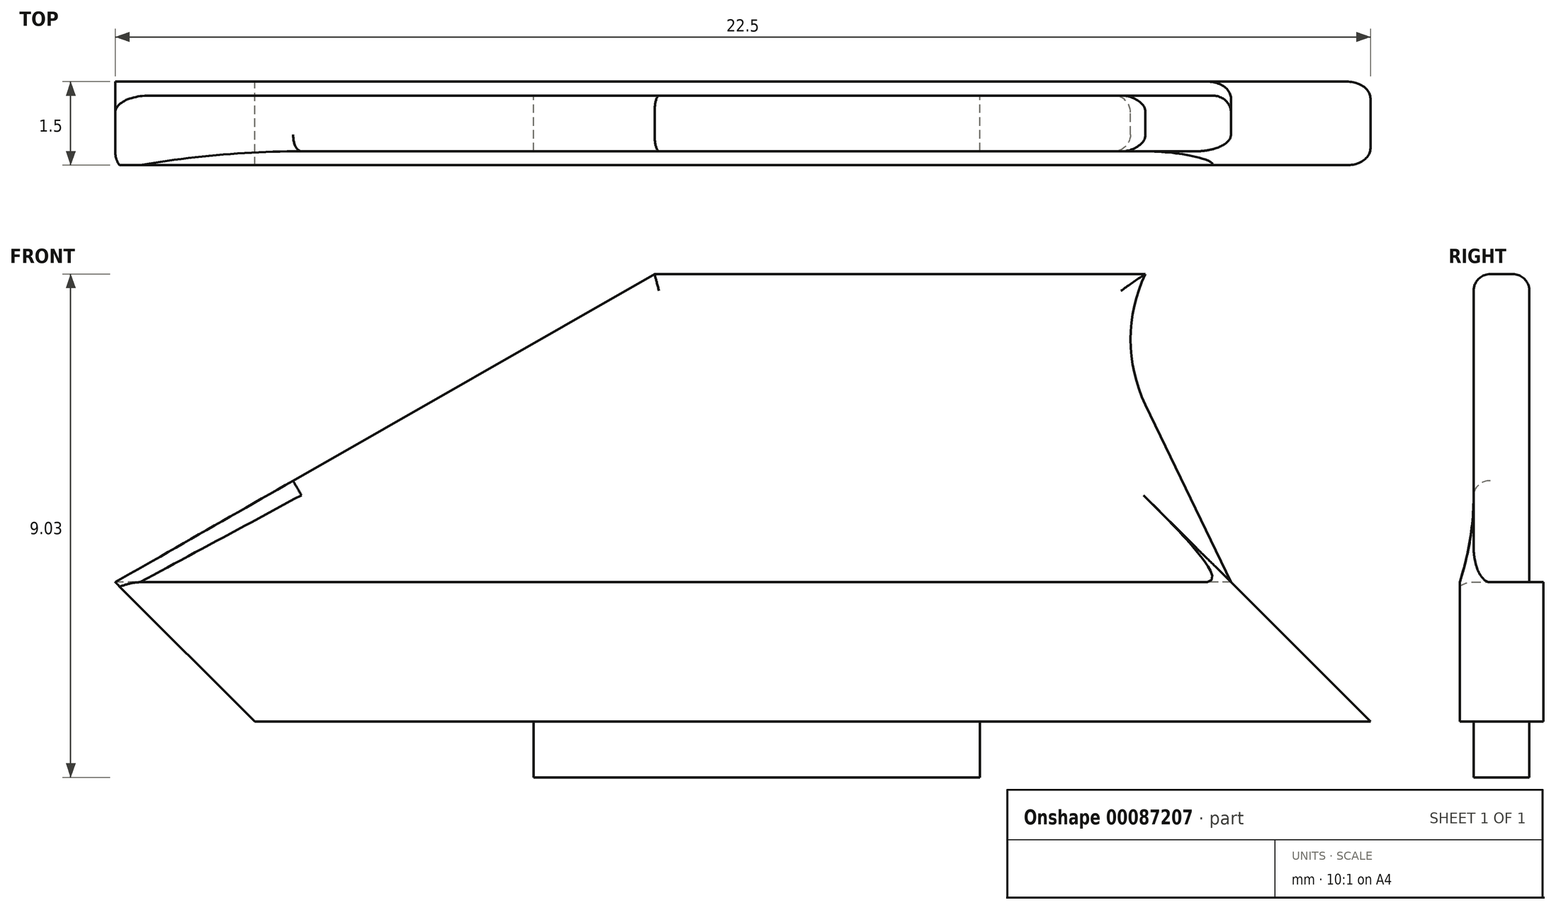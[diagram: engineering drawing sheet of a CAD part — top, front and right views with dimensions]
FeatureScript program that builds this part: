
annotation { "Feature Type Name" : "Feature", "Feature Type Description" : "" }
export const myFeature = defineFeature(function(context is Context, id is Id, definition is map)
    precondition{}
    {
        {
            var Q0;
            Q0=qCreatedBy(makeId("Front.planeOp"),FACE);
            var sketch = newSketch(context, id + "F0", { "sketchPlane" : qUnion([Q0])});
            skLineSegment(sketch, "E0", {"start": v(0, 0) * mm, "end": v(-20, 0) * mm});
            skLineSegment(sketch, "E1", {"start": v(-22.5, 2.5) * mm, "end": v(-20, 0) * mm});
            skLineSegment(sketch, "E2", {"start": v(-22.5, 2.5) * mm, "end": v(-2.5, 2.5) * mm});
            skLineSegment(sketch, "E3", {"start": v(-2.5, 2.5) * mm, "end": v(0, 0) * mm});
            skSolve(sketch);
        }
        {
            var Q0;
            Q0 = qSketchRegion(id + "F0", true);
            extrude(context, id + "F1", {"entities" : qUnion([Q0]), "endBound" : BoundingType.SYMMETRIC, "depth" : 1.5 * mm});
        }
        {
            var Q0;
            Q0=makeQuery(id+"F1.opExtrude","CAP_EDGE",EDGE,{"disambiguationData":[OSD([sQuery(id+"F0.wireOp",EDGE,"E3")])],"isStart":true});
            var Q1;
            Q1=makeQuery(id+"F1.opExtrude","CAP_EDGE",EDGE,{"disambiguationData":[OSD([sQuery(id+"F0.wireOp",EDGE,"E3")])],"isStart":false});
            fillet(context, id + "F2", {"entities" : qUnion([Q0, Q1]), "radius" : .3 * mm, "tangentPropagation" : true, "allowEdgeOverflow" : false});
        }
        {
            var Q0;
            Q0=qCreatedBy(makeId("Front.planeOp"),FACE);
            var sketch = newSketch(context, id + "F3", { "sketchPlane" : qUnion([Q0])});
            skLineSegment(sketch, "E4", {"start": v(0, 0) * mm, "end": v(-20, 0) * mm});
            skLineSegment(sketch, "E5", {"start": v(-20, 0) * mm, "end": v(-20, 2.5) * mm});
            skLineSegment(sketch, "E6", {"start": v(-20, 2.5) * mm, "end": v(-22.5, 2.5) * mm});
            skLineSegment(sketch, "E7", {"start": v(-12.83, 8.03) * mm, "end": v(-4.03, 8.03) * mm});
            skLineSegment(sketch, "E8", {"start": v(-22.5, 2.5) * mm, "end": v(-12.83, 8.03) * mm});
            skLineSegment(sketch, "E9", {"start": v(-22.5, 2.5) * mm, "end": v(-2.5, 2.5) * mm});
            skLineSegment(sketch, "E10.filletArc", {"start": v(-12.83, 8.03) * mm, "end": v(-12.83, 8.03) * mm});
            skLineSegment(sketch, "E11", {"start": v(-4.03, 5.69) * mm, "end": v(-2.5, 2.5) * mm});
            skArc(sketch, "E12", {"start": v(-4.03, 8.03) * mm, "mid": v(-4.3, 6.86) * mm, "end": v(-4.03, 5.69) * mm});
            skSolve(sketch);
        }
        {
            var Q0;
            Q0 = qSketchRegion(id + "F3", true);
            extrude(context, id + "F4", {"entities" : qUnion([Q0]), "operationType" : NewBodyOperationType.ADD, "endBound" : BoundingType.SYMMETRIC, "depth" : 1 * mm});
        }
        {
            var Q0;
            Q0=makeQuery(id+"F4.opExtrude","CAP_EDGE",EDGE,{"disambiguationData":[OSD([sQuery(id+"F3.wireOp",EDGE,"E9")])],"isStart":false});
            var Q1;
            Q1=makeQuery(id+"F4.opExtrude","CAP_EDGE",EDGE,{"disambiguationData":[OSD([sQuery(id+"F3.wireOp",EDGE,"E9")])],"isStart":true});
            fillet(context, id + "F5", {"entities" : qUnion([Q0, Q1]), "radius" : 5 * mm, "tangentPropagation" : true, "allowEdgeOverflow" : false});
        }
        {
            var Q0;
            Q0=makeQuery(id+"F5.opFillet","BLEND_EDGE",EDGE,{"blendedFrom":[makeQuery(id+"F4.opExtrude","CAP_EDGE",EDGE,{"disambiguationData":[OSD([sQuery(id+"F3.wireOp",EDGE,"E9")])],"isStart":false}),makeQuery(id+"F4.opExtrude","SWEPT_FACE",FACE,{"disambiguationData":[OSD([sQuery(id+"F3.wireOp",EDGE,"E8")])]})],"blendedInto":[makeQuery(id+"F4.opExtrude","SWEPT_FACE",FACE,{"disambiguationData":[OSD([sQuery(id+"F3.wireOp",EDGE,"E8")])]})]});
            var Q1;
            Q1=makeQuery(id+"F4.opExtrude","CAP_EDGE",EDGE,{"disambiguationData":[OSD([sQuery(id+"F3.wireOp",EDGE,"E8")])],"isStart":false});
            var Q2;
            Q2=makeQuery(id+"F4.opExtrude","CAP_EDGE",EDGE,{"disambiguationData":[OSD([sQuery(id+"F3.wireOp",EDGE,"E7")])],"isStart":false});
            var Q3;
            Q3=makeQuery(id+"F4.opExtrude","CAP_EDGE",EDGE,{"disambiguationData":[OSD([sQuery(id+"F3.wireOp",EDGE,"E12")])],"isStart":false});
            var Q4;
            Q4=makeQuery(id+"F4.opExtrude","CAP_EDGE",EDGE,{"disambiguationData":[OSD([sQuery(id+"F3.wireOp",EDGE,"E11")])],"isStart":false});
            var Q5;
            Q5=makeQuery(id+"F5.opFillet","BLEND_EDGE",EDGE,{"blendedFrom":[makeQuery(id+"F4.opExtrude","CAP_EDGE",EDGE,{"disambiguationData":[OSD([sQuery(id+"F3.wireOp",EDGE,"E9")])],"isStart":false}),makeQuery(id+"F4.opExtrude","SWEPT_FACE",FACE,{"disambiguationData":[OSD([sQuery(id+"F3.wireOp",EDGE,"E11")])]})],"blendedInto":[makeQuery(id+"F4.opExtrude","SWEPT_FACE",FACE,{"disambiguationData":[OSD([sQuery(id+"F3.wireOp",EDGE,"E11")])]})]});
            var Q6;
            Q6=makeQuery(id+"F5.opFillet","BLEND_EDGE",EDGE,{"blendedFrom":[makeQuery(id+"F4.opExtrude","CAP_EDGE",EDGE,{"disambiguationData":[OSD([sQuery(id+"F3.wireOp",EDGE,"E9")])],"isStart":true}),makeQuery(id+"F4.opExtrude","SWEPT_FACE",FACE,{"disambiguationData":[OSD([sQuery(id+"F3.wireOp",EDGE,"E11")])]})],"blendedInto":[makeQuery(id+"F4.opExtrude","SWEPT_FACE",FACE,{"disambiguationData":[OSD([sQuery(id+"F3.wireOp",EDGE,"E11")])]})]});
            var Q7;
            Q7=makeQuery(id+"F4.opExtrude","CAP_EDGE",EDGE,{"disambiguationData":[OSD([sQuery(id+"F3.wireOp",EDGE,"E11")])],"isStart":true});
            var Q8;
            Q8=makeQuery(id+"F4.opExtrude","CAP_EDGE",EDGE,{"disambiguationData":[OSD([sQuery(id+"F3.wireOp",EDGE,"E12")])],"isStart":true});
            var Q9;
            Q9=makeQuery(id+"F4.opExtrude","CAP_EDGE",EDGE,{"disambiguationData":[OSD([sQuery(id+"F3.wireOp",EDGE,"E7")])],"isStart":true});
            var Q10;
            Q10=makeQuery(id+"F4.opExtrude","CAP_EDGE",EDGE,{"disambiguationData":[OSD([sQuery(id+"F3.wireOp",EDGE,"E8")])],"isStart":true});
            var Q11;
            Q11=makeQuery(id+"F5.opFillet","BLEND_EDGE",EDGE,{"blendedFrom":[makeQuery(id+"F4.opExtrude","CAP_EDGE",EDGE,{"disambiguationData":[OSD([sQuery(id+"F3.wireOp",EDGE,"E9")])],"isStart":true}),makeQuery(id+"F4.opExtrude","SWEPT_FACE",FACE,{"disambiguationData":[OSD([sQuery(id+"F3.wireOp",EDGE,"E8")])]})],"blendedInto":[makeQuery(id+"F4.opExtrude","SWEPT_FACE",FACE,{"disambiguationData":[OSD([sQuery(id+"F3.wireOp",EDGE,"E8")])]})]});
            fillet(context, id + "F6", {"entities" : qUnion([Q0, Q1, Q2, Q3, Q4, Q5, Q6, Q7, Q8, Q9, Q10, Q11]), "radius" : .3 * mm, "tangentPropagation" : true, "allowEdgeOverflow" : false});
        }
        {
            var Q0;
            Q0=qCreatedBy(makeId("Front.planeOp"),FACE);
            var sketch = newSketch(context, id + "F7", { "sketchPlane" : qUnion([Q0])});
            skLineSegment(sketch, "E13", {"start": v(0, 0) * mm, "end": v(-7, 0) * mm});
            skLineSegment(sketch, "E14", {"start": v(-7, 0) * mm, "end": v(-15, 0) * mm});
            skLineSegment(sketch, "E15", {"start": v(-15, 0) * mm, "end": v(-15, -1) * mm});
            skLineSegment(sketch, "E16", {"start": v(-15, -1) * mm, "end": v(-7, -1) * mm});
            skLineSegment(sketch, "E17", {"start": v(-7, -1) * mm, "end": v(-7, 0) * mm});
            skSolve(sketch);
        }
        {
            var Q0;
            Q0=makeQuery(id+"F7.imprint","IMPRINT",FACE,{"disambiguationData":[TD([[makeQuery(id+"F7.imprint","IMPRINT",EDGE,{"derivedFrom":sQuery(id+"F7.wireOp",EDGE,"E14")}),1.0]])]});
            extrude(context, id + "F8", {"entities" : qUnion([Q0]), "endBound" : BoundingType.SYMMETRIC, "depth" : 1 * mm});
        }
    });
